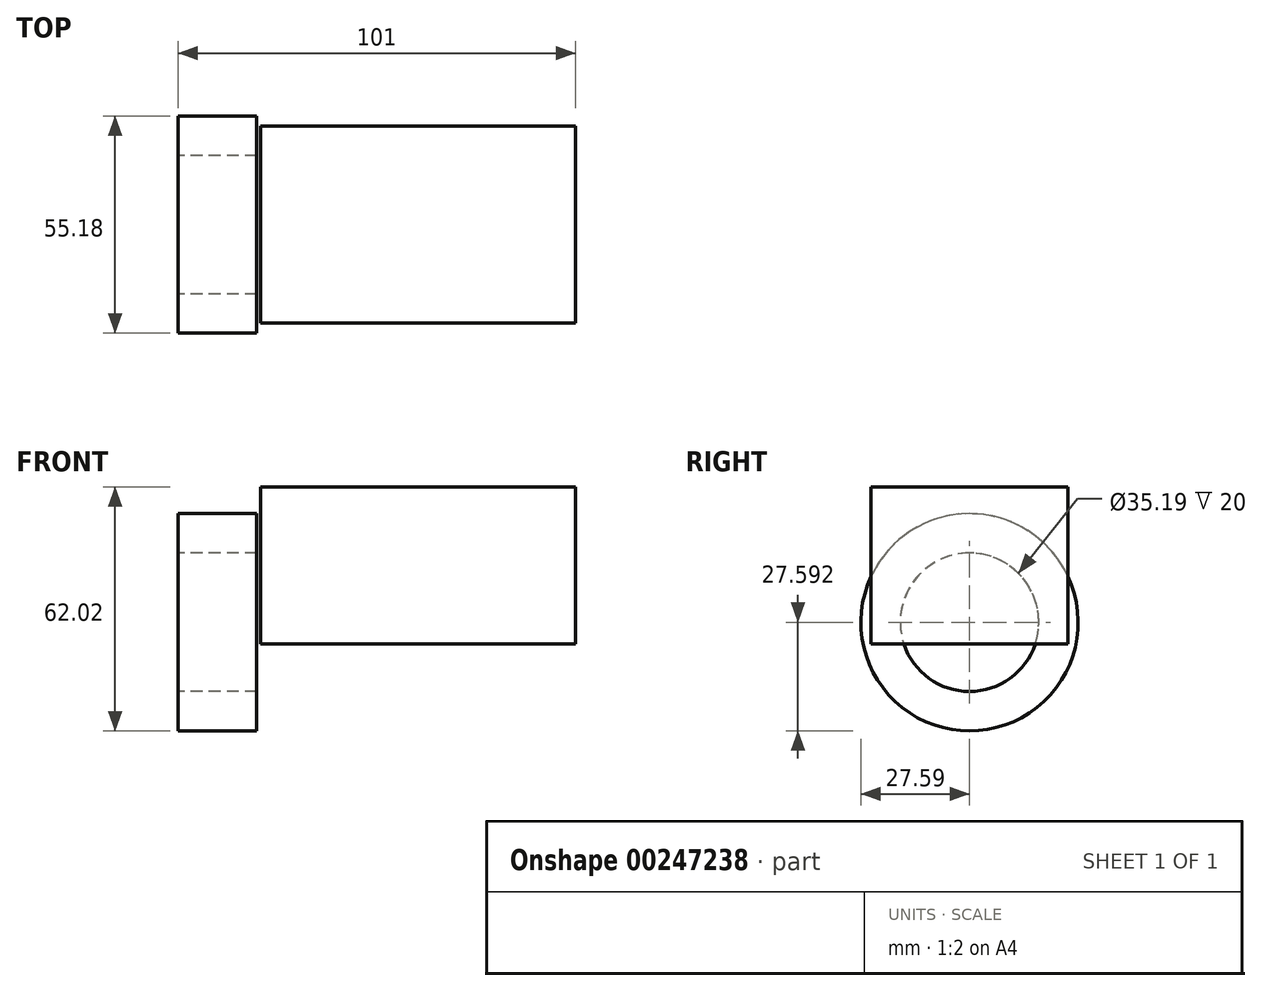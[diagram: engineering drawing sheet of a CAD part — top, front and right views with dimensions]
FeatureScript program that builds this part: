
annotation { "Feature Type Name" : "Feature", "Feature Type Description" : "" }
export const myFeature = defineFeature(function(context is Context, id is Id, definition is map)
    precondition{}
    {
        {
            var Q0;
            Q0=qCreatedBy(makeId("Top.planeOp"),FACE);
            var sketch = newSketch(context, id + "F0", { "sketchPlane" : qUnion([Q0])});
            skLineSegment(sketch, "E0.bottom", {"start": v(-40, 25) * mm, "end": v(40, 25) * mm});
            skLineSegment(sketch, "E0.top", {"start": v(-40, -25) * mm, "end": v(40, -25) * mm});
            skLineSegment(sketch, "E0.left", {"start": v(-40, 25) * mm, "end": v(-40, -25) * mm});
            skLineSegment(sketch, "E0.right", {"start": v(40, 25) * mm, "end": v(40, -25) * mm});
            skPoint(sketch, "E0.middle", {"position": v(0, 0) * mm});
            skSolve(sketch);
        }
        {
            var Q0;
            Q0 = qSketchRegion(id + "F0", true);
            var Q1;
            Q1=makeQuery(id+"F0.imprint","IMPRINT",FACE,{"disambiguationData":[TD([[makeQuery(id+"F0.imprint","IMPRINT",EDGE,{"derivedFrom":sQuery(id+"F0.wireOp",EDGE,"E0.bottom")}),-1.0]])]});
            extrude(context, id + "F1", {"entities" : qUnion([Q0, Q1]), "endBound" : BoundingType.SYMMETRIC, "depth" : 40 * mm});
        }
        {
            var Q0;
            Q0=qCreatedBy(makeId("Right.planeOp"),FACE);
            var sketch = newSketch(context, id + "F2", { "sketchPlane" : qUnion([Q0])});
            skLineSegment(sketch, "E1", {"start": v(59.46, 0) * mm, "end": v(-74, 0) * mm, "construction": true});
            skSolve(sketch);
        }
        {
            var Q0;
            Q0=qCreatedBy(makeId("Front.planeOp"),FACE);
            var sketch = newSketch(context, id + "F3", { "sketchPlane" : qUnion([Q0])});
            skLineSegment(sketch, "E2.bottom", {"start": v(-41, 3.17) * mm, "end": v(-61, 3.17) * mm});
            skLineSegment(sketch, "E2.top", {"start": v(-41, 13.17) * mm, "end": v(-61, 13.17) * mm});
            skLineSegment(sketch, "E2.left", {"start": v(-41, 3.17) * mm, "end": v(-41, 13.17) * mm});
            skLineSegment(sketch, "E2.right", {"start": v(-61, 3.17) * mm, "end": v(-61, 13.17) * mm});
            skPoint(sketch, "E2.middle", {"position": v(-51, 8.17) * mm});
            skSolve(sketch);
        }
        {
            var Q0;
            Q0=qCreatedBy(makeId("Front.planeOp"),FACE);
            var sketch = newSketch(context, id + "F4", { "sketchPlane" : qUnion([Q0])});
            skLineSegment(sketch, "E3", {"start": v(-62.92, -14.43) * mm, "end": v(59.37, -14.43) * mm, "construction": true});
            skSolve(sketch);
        }
        {
            var Q0;
            Q0=makeQuery(id+"F3.imprint","IMPRINT",FACE,{"disambiguationData":[TD([[makeQuery(id+"F3.imprint","IMPRINT",EDGE,{"derivedFrom":sQuery(id+"F3.wireOp",EDGE,"E2.bottom")}),-1.0]])]});
            var Q1;
            Q1=sQuery(id+"F4.wireOp",EDGE,"E3");
            revolve(context, id + "F5", {"entities" : qUnion([Q0]), "axis" : qUnion([Q1]), "revolveType" : RevolveType.FULL});
        }
    });
